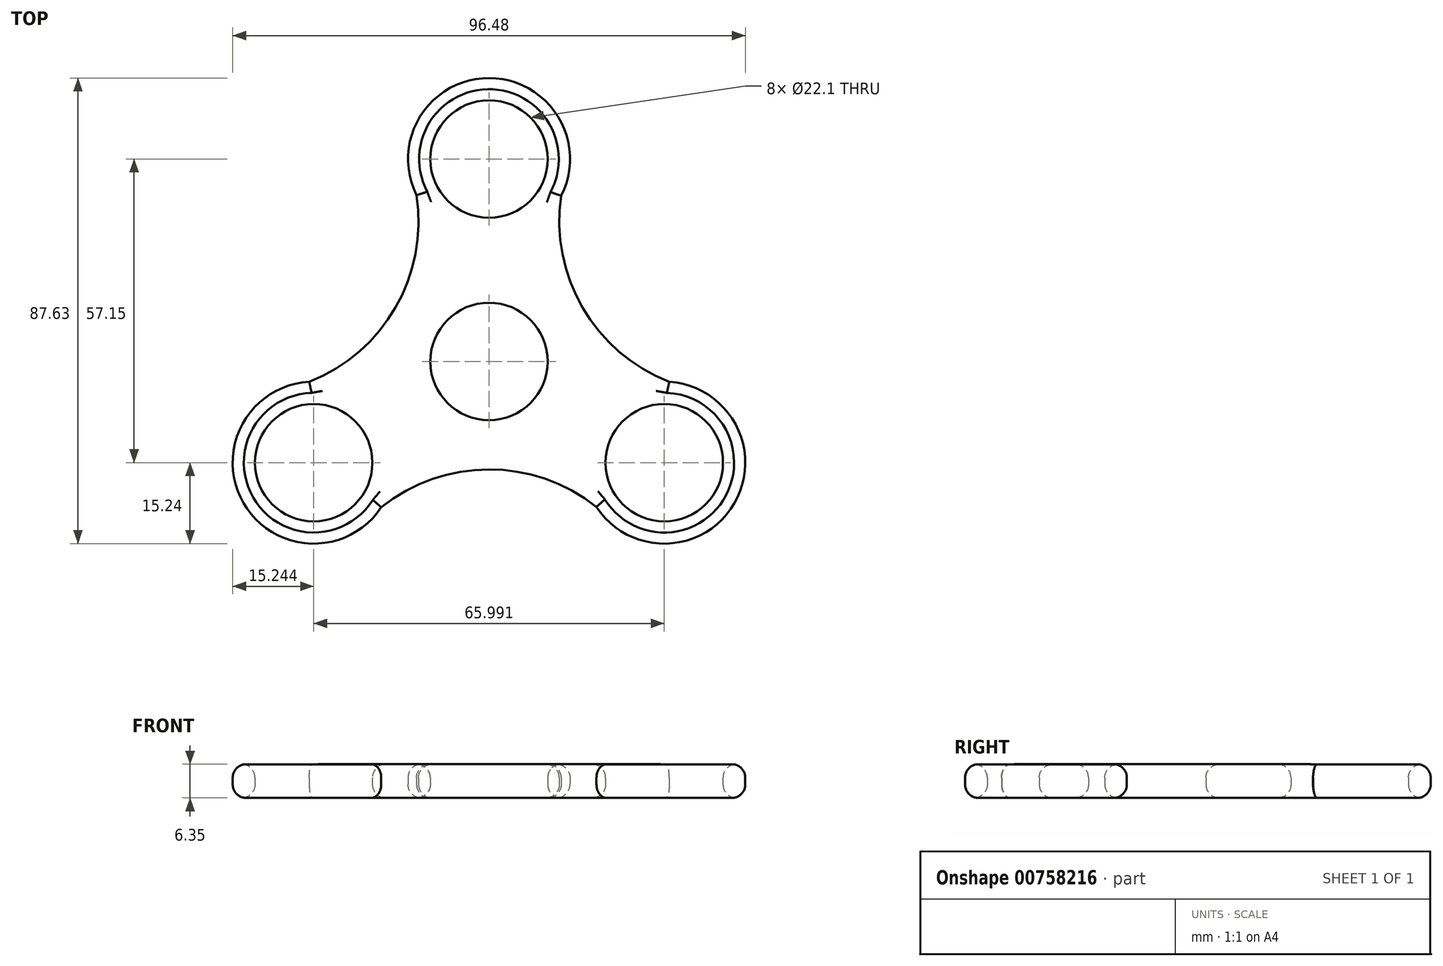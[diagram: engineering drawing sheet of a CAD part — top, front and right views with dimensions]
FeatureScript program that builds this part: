
annotation { "Feature Type Name" : "Feature", "Feature Type Description" : "" }
export const myFeature = defineFeature(function(context is Context, id is Id, definition is map)
    precondition{}
    {
        {
            var Q0;
            Q0=qCreatedBy(makeId("Top.planeOp"),FACE);
            var sketch = newSketch(context, id + "F0", { "sketchPlane" : qUnion([Q0])});
            skCircle(sketch, "E0", {"center": v(0, 0) * mm, "radius": 11.05 * mm});
            skCircle(sketch, "E1", {"center": v(0, 38.1) * mm, "radius": 11.05 * mm});
            skArc(sketch, "E2", {"start": v(13.6, 31.2) * mm, "mid": v(0.05, 53.34) * mm, "end": v(-13.64, 31.3) * mm});
            skCircle(sketch, "E3.1.0", {"center": v(-33, -19.05) * mm, "radius": 11.05 * mm});
            skArc(sketch, "E3.1.1", {"start": v(-33.82, -3.83) * mm, "mid": v(-46.22, -26.63) * mm, "end": v(-20.28, -27.46) * mm});
            skCircle(sketch, "E3.2.0", {"center": v(33, -19.05) * mm, "radius": 11.05 * mm});
            skArc(sketch, "E3.2.1", {"start": v(20.23, -27.38) * mm, "mid": v(46.17, -26.71) * mm, "end": v(33.92, -3.84) * mm});
            skArc(sketch, "E4", {"start": v(-33.82, -3.83) * mm, "mid": v(-17.57, 10.2) * mm, "end": v(-13.64, 31.3) * mm});
            skArc(sketch, "E5.1.0", {"start": v(20.23, -27.38) * mm, "mid": v(-0.04, -20.32) * mm, "end": v(-20.28, -27.46) * mm});
            skArc(sketch, "E5.2.0", {"start": v(13.6, 31.2) * mm, "mid": v(17.61, 10.12) * mm, "end": v(33.92, -3.84) * mm});
            skSolve(sketch);
        }
        {
            var Q0;
            Q0=qSketchRegion(id+"F0",true);
            extrude(context, id + "F1", {"entities" : qUnion([Q0]), "depth" : 6.35 * mm, "offsetDistance" : 25.4 * mm});
        }
        {
            var Q0;
            Q0=makeQuery(id+"F1.opExtrude","CAP_FACE",FACE,{"disambiguationData":[OSD([sQuery(id+"F0.wireOp",EDGE,"E0"),sQuery(id+"F0.wireOp",EDGE,"E1"),sQuery(id+"F0.wireOp",EDGE,"E2"),sQuery(id+"F0.wireOp",EDGE,"E3.1.0"),sQuery(id+"F0.wireOp",EDGE,"E3.1.1"),sQuery(id+"F0.wireOp",EDGE,"E3.2.0"),sQuery(id+"F0.wireOp",EDGE,"E3.2.1"),sQuery(id+"F0.wireOp",EDGE,"E4"),sQuery(id+"F0.wireOp",EDGE,"E5.1.0"),sQuery(id+"F0.wireOp",EDGE,"E5.2.0")])],"isStart":false});
            var Q1;
            Q1=makeQuery(id+"F1.opExtrude","CAP_FACE",FACE,{"disambiguationData":[OSD([sQuery(id+"F0.wireOp",EDGE,"E0"),sQuery(id+"F0.wireOp",EDGE,"E1"),sQuery(id+"F0.wireOp",EDGE,"E2"),sQuery(id+"F0.wireOp",EDGE,"E3.1.0"),sQuery(id+"F0.wireOp",EDGE,"E3.1.1"),sQuery(id+"F0.wireOp",EDGE,"E3.2.0"),sQuery(id+"F0.wireOp",EDGE,"E3.2.1"),sQuery(id+"F0.wireOp",EDGE,"E4"),sQuery(id+"F0.wireOp",EDGE,"E5.1.0"),sQuery(id+"F0.wireOp",EDGE,"E5.2.0")])],"isStart":true});
            fillet(context, id + "F2", {"entities" : qUnion([Q0, Q1]), "radius" : 2.54 * mm, "tangentPropagation" : true, "allowEdgeOverflow" : false});
        }
    });
